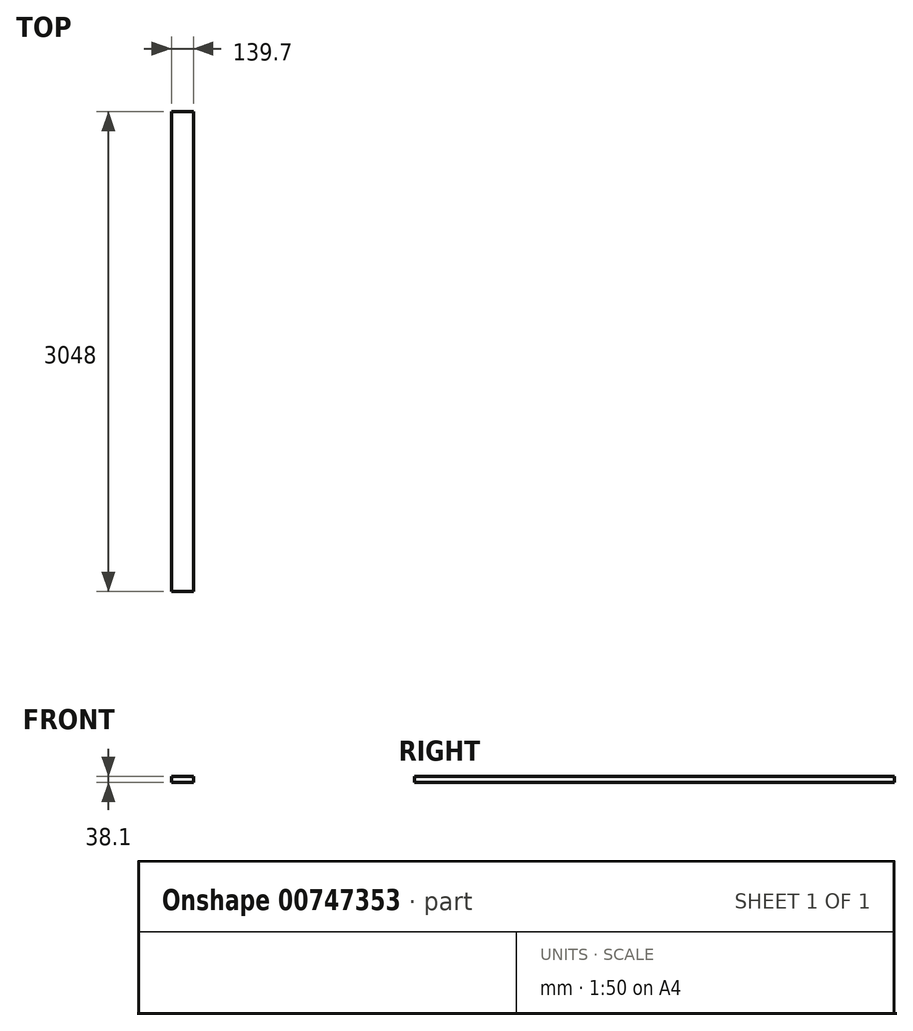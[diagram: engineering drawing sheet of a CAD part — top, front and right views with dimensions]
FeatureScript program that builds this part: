
annotation { "Feature Type Name" : "Feature", "Feature Type Description" : "" }
export const myFeature = defineFeature(function(context is Context, id is Id, definition is map)
    precondition{}
    {
        {
            var Q0;
            Q0=qCreatedBy(makeId("Front.planeOp"),FACE);
            var sketch = newSketch(context, id + "F0", { "sketchPlane" : qUnion([Q0])});
            skLineSegment(sketch, "E0.bottom", {"start": v(0, 0) * mm, "end": v(139.7, 0) * mm});
            skLineSegment(sketch, "E0.top", {"start": v(0, 38.1) * mm, "end": v(139.7, 38.1) * mm});
            skLineSegment(sketch, "E0.left", {"start": v(0, 0) * mm, "end": v(0, 38.1) * mm});
            skLineSegment(sketch, "E0.right", {"start": v(139.7, 0) * mm, "end": v(139.7, 38.1) * mm});
            skSolve(sketch);
        }
        {
            var Q0;
            Q0=qSketchRegion(id+"F0",true);
            extrude(context, id + "F1", {"entities" : qUnion([Q0]), "depth" : 3048 * mm, "offsetDistance" : 25.4 * mm});
        }
    });
